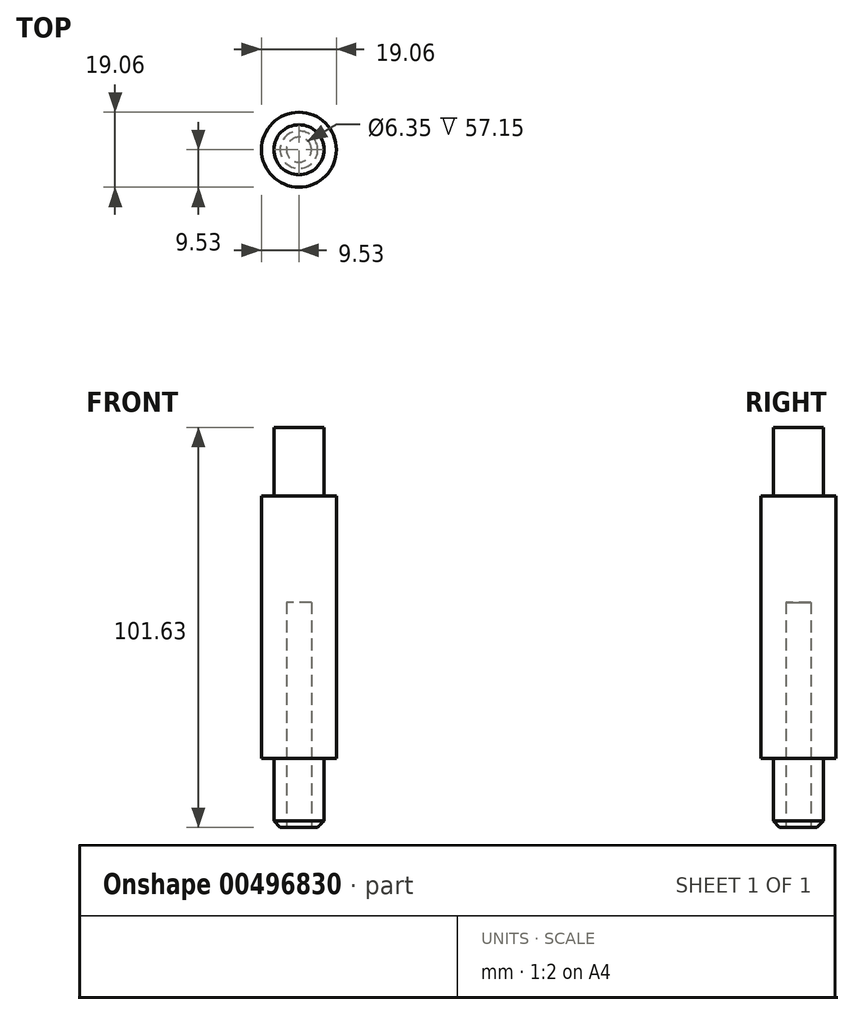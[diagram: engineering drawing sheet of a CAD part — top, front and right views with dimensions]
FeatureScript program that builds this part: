
annotation { "Feature Type Name" : "Feature", "Feature Type Description" : "" }
export const myFeature = defineFeature(function(context is Context, id is Id, definition is map)
    precondition{}
    {
        {
            var Q0;
            Q0=qCreatedBy(makeId("Top.planeOp"),FACE);
            var sketch = newSketch(context, id + "F0", { "sketchPlane" : qUnion([Q0])});
            skCircle(sketch, "E0", {"center": v(0, 0) * mm, "radius": 9.53 * mm});
            skCircle(sketch, "E1", {"center": v(0, 0) * mm, "radius": 6.35 * mm});
            skCircle(sketch, "E2", {"center": v(0, 0) * mm, "radius": 3.18 * mm});
            skSolve(sketch);
        }
        {
            var Q0;
            Q0=makeQuery(id+"F0.imprint","IMPRINT",FACE,{"disambiguationData":[TD([[makeQuery(id+"F0.imprint","IMPRINT",EDGE,{"derivedFrom":sQuery(id+"F0.wireOp",EDGE,"E0")}),1.0]])]});
            extrude(context, id + "F1", {"entities" : qUnion([Q0]), "depth" : 66.67 * mm});
        }
        {
            var Q0;
            Q0=makeQuery(id+"F0.imprint","IMPRINT",FACE,{"disambiguationData":[TD([[makeQuery(id+"F0.imprint","IMPRINT",EDGE,{"derivedFrom":sQuery(id+"F0.wireOp",EDGE,"E1")}),1.0]])]});
            extrude(context, id + "F2", {"entities" : qUnion([Q0]), "operationType" : NewBodyOperationType.ADD, "depth" : 84.15 * mm});
        }
        {
            var Q0;
            Q0=makeQuery(id+"F0.imprint","IMPRINT",FACE,{"disambiguationData":[TD([[makeQuery(id+"F0.imprint","IMPRINT",EDGE,{"derivedFrom":sQuery(id+"F0.wireOp",EDGE,"E1")}),1.0]])]});
            extrude(context, id + "F3", {"entities" : qUnion([Q0]), "operationType" : NewBodyOperationType.ADD, "oppositeDirection" : true, "depth" : 17.48 * mm});
        }
        {
            var Q0;
            Q0=makeQuery(id+"F3.opExtrude","CAP_EDGE",EDGE,{"disambiguationData":[OSD([sQuery(id+"F0.wireOp",EDGE,"E1")])],"isStart":false});
            chamfer(context, id + "F4", {"entities" : qUnion([Q0]), "width" : 1.59 * mm, "tangentPropagation" : true});
        }
        {
            var Q0;
            Q0=makeQuery(id+"F2.opExtrude","CAP_FACE",FACE,{"disambiguationData":[OSD([sQuery(id+"F0.wireOp",EDGE,"E1"),sQuery(id+"F0.wireOp",EDGE,"E2")])],"isStart":false});
            var sketch = newSketch(context, id + "F5", { "sketchPlane" : qUnion([Q0])});
            skSolve(sketch);
        }
        {
            var Q0;
            Q0=makeQuery(id+"F5.imprint","IMPRINT",FACE,{"disambiguationData":[TD([[makeQuery(id+"F5.imprint","IMPRINT",EDGE,{"derivedFrom":makeQuery(id+"F2.opExtrude","CAP_EDGE",EDGE,{"disambiguationData":[OSD([sQuery(id+"F0.wireOp",EDGE,"E2")])],"isStart":false})}),1.0]])]});
            extrude(context, id + "F6", {"entities" : qUnion([Q0]), "operationType" : NewBodyOperationType.ADD, "oppositeDirection" : true, "depth" : 44.48 * mm});
        }
    });
